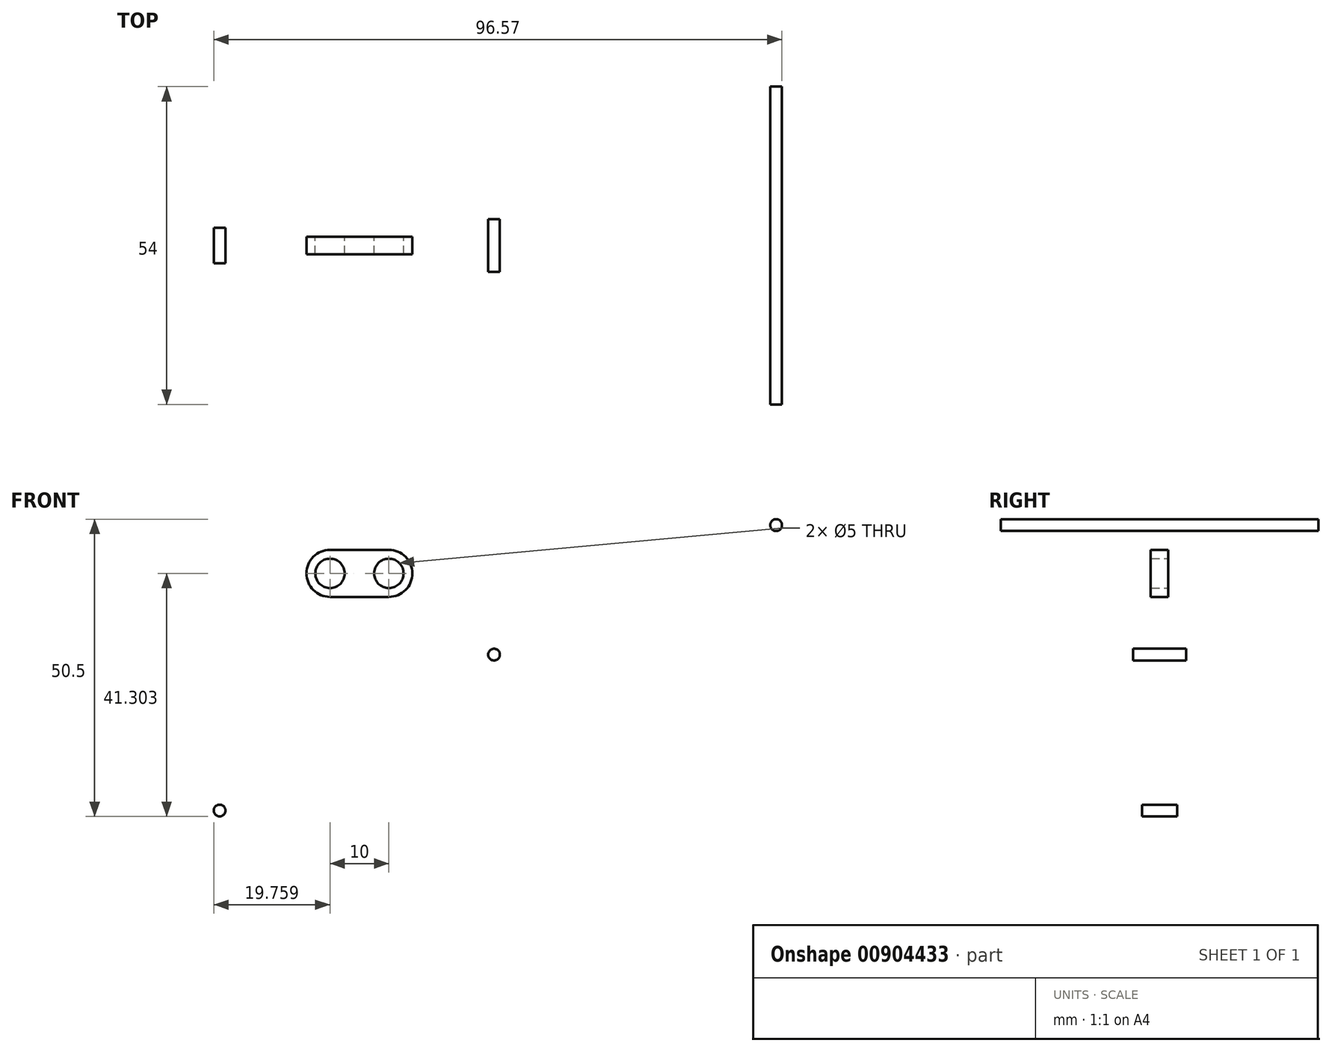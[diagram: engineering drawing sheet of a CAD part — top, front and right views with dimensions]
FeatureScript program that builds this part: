
annotation { "Feature Type Name" : "Feature", "Feature Type Description" : "" }
export const myFeature = defineFeature(function(context is Context, id is Id, definition is map)
    precondition{}
    {
        {
            var Q0;
            Q0=qCreatedBy(makeId("Front.planeOp"),FACE);
            var sketch = newSketch(context, id + "F0", { "sketchPlane" : qUnion([Q0])});
            skLineSegment(sketch, "E0.bottom", {"start": v(-27.87, 9.8) * mm, "end": v(-17.87, 9.8) * mm});
            skLineSegment(sketch, "E0.top", {"start": v(-27.87, 17.8) * mm, "end": v(-17.87, 17.8) * mm});
            skLineSegment(sketch, "E0.left", {"start": v(-27.87, 9.8) * mm, "end": v(-27.87, 17.8) * mm});
            skLineSegment(sketch, "E0.right", {"start": v(-17.87, 9.8) * mm, "end": v(-17.87, 17.8) * mm});
            skArc(sketch, "E1", {"start": v(-27.87, 17.8) * mm, "mid": v(-31.87, 13.8) * mm, "end": v(-27.87, 9.8) * mm});
            skArc(sketch, "E2", {"start": v(-17.87, 9.8) * mm, "mid": v(-13.87, 13.8) * mm, "end": v(-17.87, 17.8) * mm});
            skCircle(sketch, "E3", {"center": v(-17.87, 13.8) * mm, "radius": 2.5 * mm});
            skCircle(sketch, "E4", {"center": v(-27.87, 13.8) * mm, "radius": 2.5 * mm});
            skSolve(sketch);
        }
        {
            var Q0;
            {var subQ5=sQuery(id+"F0.wireOp",EDGE,"E0.bottom");Q0=makeQuery(id+"F0.imprint","IMPRINT",FACE,{"disambiguationData":[TD([[makeQuery(id+"F0.imprint","IMPRINT",EDGE,{"derivedFrom":subQ5}),1.0]])]});}
            var Q1;
            {var subQ0=sQuery(id+"F0.wireOp",EDGE,"E2");Q1=makeQuery(id+"F0.imprint","IMPRINT",FACE,{"disambiguationData":[TD([[makeQuery(id+"F0.imprint","IMPRINT",EDGE,{"derivedFrom":subQ0}),1.0]])]});}
            var Q2;
            {var subQ0=sQuery(id+"F0.wireOp",EDGE,"E1");Q2=makeQuery(id+"F0.imprint","IMPRINT",FACE,{"disambiguationData":[TD([[makeQuery(id+"F0.imprint","IMPRINT",EDGE,{"derivedFrom":subQ0}),1.0]])]});}
            extrude(context, id + "F1", {"entities" : qUnion([Q0, Q1, Q2]), "endBound" : BoundingType.SYMMETRIC, "depth" : 3 * mm, "offsetDistance" : 25 * mm});
        }
        {
            var Q0;
            Q0=qCreatedBy(makeId("Front.planeOp"),FACE);
            var sketch = newSketch(context, id + "F2", { "sketchPlane" : qUnion([Q0])});
            skCircle(sketch, "E5", {"center": v(0, 0) * mm, "radius": 1 * mm});
            skSolve(sketch);
        }
        {
            var Q0;
            Q0=makeQuery(id+"F2.imprint","IMPRINT",FACE,{"disambiguationData":[TD([[makeQuery(id+"F2.imprint","IMPRINT",EDGE,{"derivedFrom":sQuery(id+"F2.wireOp",EDGE,"E5")}),1.0]])]});
            extrude(context, id + "F3", {"entities" : qUnion([Q0]), "endBound" : BoundingType.SYMMETRIC, "oppositeDirection" : true, "depth" : 9 * mm, "offsetDistance" : 25 * mm});
        }
        {
            var Q0;
            Q0=qCreatedBy(makeId("Front.planeOp"),FACE);
            var sketch = newSketch(context, id + "F4", { "sketchPlane" : qUnion([Q0])});
            skCircle(sketch, "E6", {"center": v(47.94, 22) * mm, "radius": 1 * mm});
            skSolve(sketch);
        }
        {
            var Q0;
            Q0=makeQuery(id+"F4.imprint","IMPRINT",FACE,{"disambiguationData":[TD([[makeQuery(id+"F4.imprint","IMPRINT",EDGE,{"derivedFrom":sQuery(id+"F4.wireOp",EDGE,"E6")}),1.0]])]});
            extrude(context, id + "F5", {"entities" : qUnion([Q0]), "endBound" : BoundingType.SYMMETRIC, "depth" : 54 * mm, "offsetDistance" : 25 * mm});
        }
        {
            var Q0;
            Q0=qCreatedBy(makeId("Front.planeOp"),FACE);
            var sketch = newSketch(context, id + "F6", { "sketchPlane" : qUnion([Q0])});
            skCircle(sketch, "E7", {"center": v(-46.63, -26.5) * mm, "radius": 1 * mm});
            skSolve(sketch);
        }
        {
            var Q0;
            Q0=makeQuery(id+"F6.imprint","IMPRINT",FACE,{"disambiguationData":[TD([[makeQuery(id+"F6.imprint","IMPRINT",EDGE,{"derivedFrom":sQuery(id+"F6.wireOp",EDGE,"E7")}),1.0]])]});
            extrude(context, id + "F7", {"entities" : qUnion([Q0]), "endBound" : BoundingType.SYMMETRIC, "depth" : 6 * mm, "offsetDistance" : 25 * mm});
        }
    });
